# Revit family: Chair-Soft_Seating-A534-Allermuir-Tommo
name_source: partatom
category: Furniture
revit_build: Autodesk Revit Architecture 2012 (Build: 20110309_2315(x64)
units: mm (PartAtom-declared; Revit-internal decimal feet)

## types (1)
- A534
    04 CSI = 12 51 00
    2.5" Casters = No
    95 CSI = 12510
    Advanced Sync Tilt with Multi Position Back = No
    Assembly Code = E2020200
    Back = Fabric - Allermuir - Smooth -Pebbled - Black
    Back frame with integral arms in a soft touch Plastic = No
    Base = Stainless - Allermuir -  Polished Brushed
    Base Type = Skid base
    Black Components = No
    Black GRP Base = No
    Black Gas Lift = No
    Black Plastic Back Membrane = No
    Brochure URL = http://www.allermuir.net
    CAD Blocks URL = http://www.allermuir.net
    Caster Options = No
    Description = High stool
    Fabric Spec Sheets = http://www.allermuir.net
    Glides = Plastic - Allermuir - Black
    Height Adjustable Arms = No
    Height Adjustable Arms with Multi funtction Pad = No
    LEED Stats URL = http://www.allermuir.net
    Lumbar Adjustment = No
    Manufacturer = Allermuir
    Manufacturer Fax = (419) 887 5805
    Model = A534
    Negative Seat Tilt = No
    Overall Depth = 19"
    Overall Height = 32 179/256"
    Overall Width = 19"
    Pedestal Base = No
    Plastic Arms in Black = No
    Plugin Data URL = http://products.ecoscorecard.com
    Polished Aluminum Arm Carrier = No
    Pricing URL = http://www.allermuir.net
    Product Line = Tommo
    Product Page URL = http://www.allermuir.net
    Seat Depth = 15 179/256"
    Seat Depth Adjustment = No
    Seat Height = 29 1/2"
    Seat Width = 16 51/256"
    Seat or Top = Fabric - Allermuir - Smooth -Pebbled - Black
    Specifications URL = http://www.allermuir.net
    Stacks = No
    Subcategory = Soft Seating
    Swaged Tubular Steel Legs = Yes
    Two Tone Upholstery = No
    URL = http://www.allermuir.net
    Upholstered Back = Yes
    Upholstered Seat = Yes
    Weight = 20.0 lb
    White Plastic Back Membrane = No
    ecoScorecard Product Page = http://products.ecoscorecard.com
    ecoScorecard_data = http://thesenatorgroup.ecoscorecard.com

## geometry (parser evidence)
native form markers: Blend x35, Sweep x4
no freeform markers — native parametric forms only
